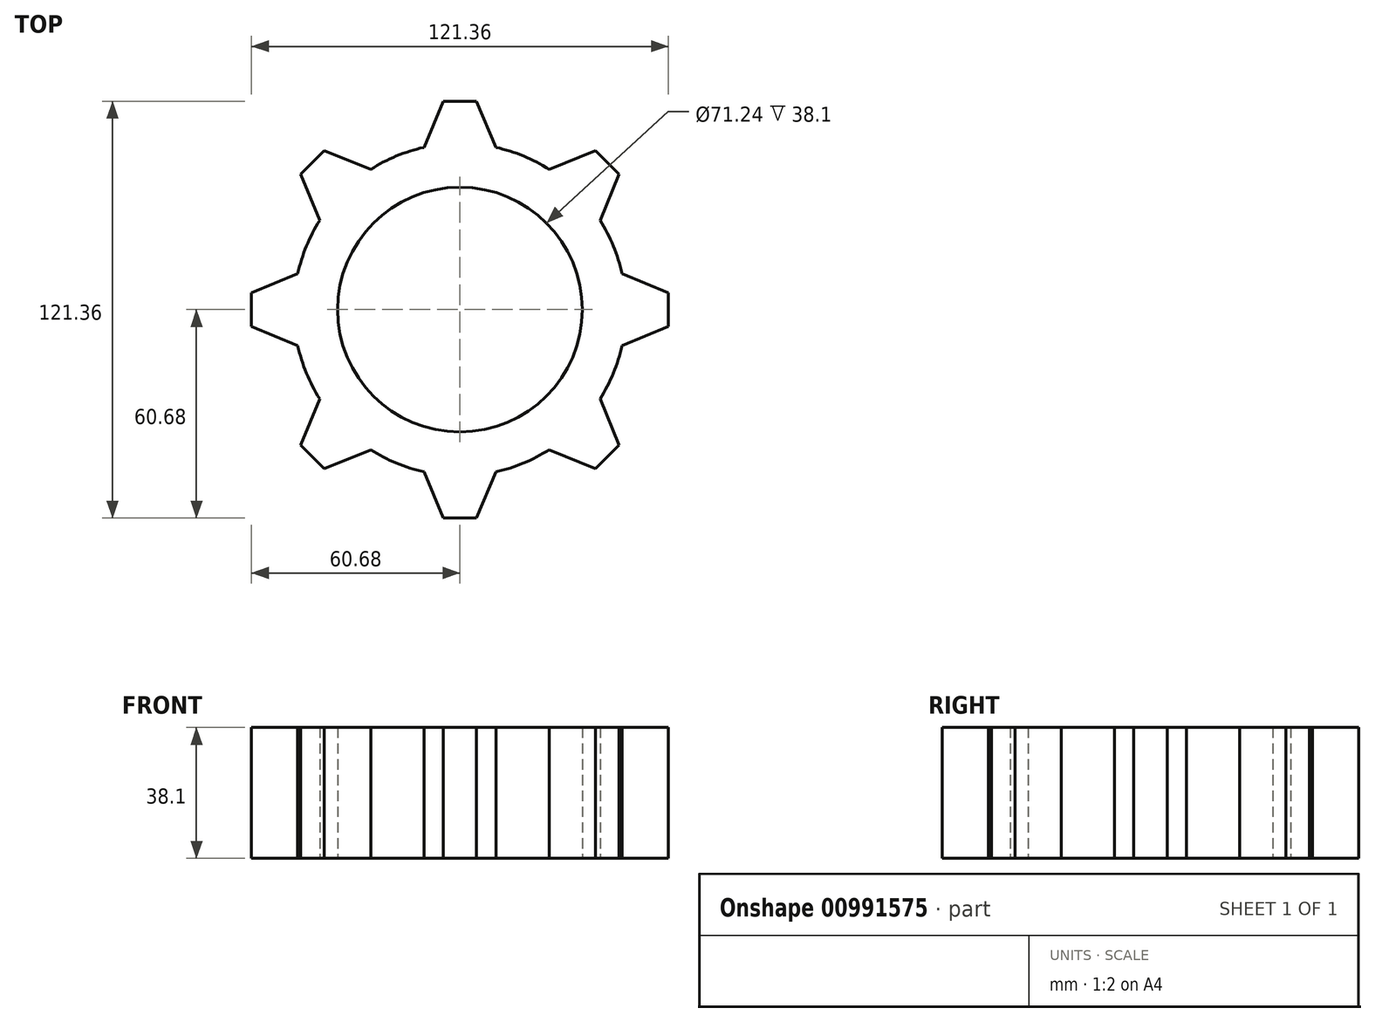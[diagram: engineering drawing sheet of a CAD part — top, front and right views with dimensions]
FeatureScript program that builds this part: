
annotation { "Feature Type Name" : "Feature", "Feature Type Description" : "" }
export const myFeature = defineFeature(function(context is Context, id is Id, definition is map)
    precondition{}
    {
        {
            var Q0;
            Q0=qCreatedBy(makeId("Top.planeOp"),FACE);
            var sketch = newSketch(context, id + "F0", { "sketchPlane" : qUnion([Q0])});
            skCircle(sketch, "E0", {"center": v(0, 0) * mm, "radius": 48.37 * mm});
            skSolve(sketch);
        }
        {
            var Q0;
            Q0=makeQuery(id+"F0.imprint","IMPRINT",FACE,{"disambiguationData":[TD([[makeQuery(id+"F0.imprint","IMPRINT",EDGE,{"derivedFrom":sQuery(id+"F0.wireOp",EDGE,"E0")}),1.0]])]});
            extrude(context, id + "F1", {"entities" : qUnion([Q0]), "depth" : 38.1 * mm, "offsetDistance" : 25.4 * mm});
        }
        {
            var Q0;
            Q0=qCreatedBy(makeId("Top.planeOp"),FACE);
            var sketch = newSketch(context, id + "F2", { "sketchPlane" : qUnion([Q0])});
            skLineSegment(sketch, "E1", {"start": v(42.15, 12.62) * mm, "end": v(60.68, 4.85) * mm});
            skLineSegment(sketch, "E2", {"start": v(60.68, 4.85) * mm, "end": v(60.68, -4.85) * mm});
            skLineSegment(sketch, "E3", {"start": v(60.68, -4.85) * mm, "end": v(42.15, -12.62) * mm});
            skLineSegment(sketch, "E4", {"start": v(42.15, -12.62) * mm, "end": v(42.15, 12.62) * mm});
            skPoint(sketch, "E5.endSnap0", {"position": v(42.15, 0) * mm});
            skLineSegment(sketch, "E6.1.0", {"start": v(39.48, 46.34) * mm, "end": v(46.34, 39.48) * mm});
            skLineSegment(sketch, "E6.1.1", {"start": v(20.88, 38.72) * mm, "end": v(39.48, 46.34) * mm});
            skLineSegment(sketch, "E6.1.2", {"start": v(46.34, 39.48) * mm, "end": v(38.72, 20.88) * mm});
            skLineSegment(sketch, "E6.1.3", {"start": v(38.72, 20.88) * mm, "end": v(20.88, 38.72) * mm});
            skLineSegment(sketch, "E6.2.0", {"start": v(-4.85, 60.68) * mm, "end": v(4.85, 60.68) * mm});
            skLineSegment(sketch, "E6.2.1", {"start": v(-12.62, 42.15) * mm, "end": v(-4.85, 60.68) * mm});
            skLineSegment(sketch, "E6.2.2", {"start": v(4.85, 60.68) * mm, "end": v(12.62, 42.15) * mm});
            skLineSegment(sketch, "E6.2.3", {"start": v(12.62, 42.15) * mm, "end": v(-12.62, 42.15) * mm});
            skLineSegment(sketch, "E6.3.0", {"start": v(-46.34, 39.48) * mm, "end": v(-39.48, 46.34) * mm});
            skLineSegment(sketch, "E6.3.1", {"start": v(-38.72, 20.88) * mm, "end": v(-46.34, 39.48) * mm});
            skLineSegment(sketch, "E6.3.2", {"start": v(-39.48, 46.34) * mm, "end": v(-20.88, 38.72) * mm});
            skLineSegment(sketch, "E6.3.3", {"start": v(-20.88, 38.72) * mm, "end": v(-38.72, 20.88) * mm});
            skLineSegment(sketch, "E6.4.0", {"start": v(-60.68, -4.85) * mm, "end": v(-60.68, 4.85) * mm});
            skLineSegment(sketch, "E6.4.1", {"start": v(-42.15, -12.62) * mm, "end": v(-60.68, -4.85) * mm});
            skLineSegment(sketch, "E6.4.2", {"start": v(-60.68, 4.85) * mm, "end": v(-42.15, 12.62) * mm});
            skLineSegment(sketch, "E6.4.3", {"start": v(-42.15, 12.62) * mm, "end": v(-42.15, -12.62) * mm});
            skLineSegment(sketch, "E6.5.0", {"start": v(-39.48, -46.34) * mm, "end": v(-46.34, -39.48) * mm});
            skLineSegment(sketch, "E6.5.1", {"start": v(-20.88, -38.72) * mm, "end": v(-39.48, -46.34) * mm});
            skLineSegment(sketch, "E6.5.2", {"start": v(-46.34, -39.48) * mm, "end": v(-38.72, -20.88) * mm});
            skLineSegment(sketch, "E6.5.3", {"start": v(-38.72, -20.88) * mm, "end": v(-20.88, -38.72) * mm});
            skLineSegment(sketch, "E6.6.0", {"start": v(4.85, -60.68) * mm, "end": v(-4.85, -60.68) * mm});
            skLineSegment(sketch, "E6.6.1", {"start": v(12.62, -42.15) * mm, "end": v(4.85, -60.68) * mm});
            skLineSegment(sketch, "E6.6.2", {"start": v(-4.85, -60.68) * mm, "end": v(-12.62, -42.15) * mm});
            skLineSegment(sketch, "E6.6.3", {"start": v(-12.62, -42.15) * mm, "end": v(12.62, -42.15) * mm});
            skLineSegment(sketch, "E6.7.0", {"start": v(46.34, -39.48) * mm, "end": v(39.48, -46.34) * mm});
            skLineSegment(sketch, "E6.7.1", {"start": v(38.72, -20.88) * mm, "end": v(46.34, -39.48) * mm});
            skLineSegment(sketch, "E6.7.2", {"start": v(39.48, -46.34) * mm, "end": v(20.88, -38.72) * mm});
            skLineSegment(sketch, "E6.7.3", {"start": v(20.88, -38.72) * mm, "end": v(38.72, -20.88) * mm});
            skPoint(sketch, "E6.center", {"position": v(0, 0) * mm});
            skSolve(sketch);
        }
        {
            var Q0;
            Q0=makeQuery(id+"F2.imprint","IMPRINT",FACE,{"disambiguationData":[TD([[makeQuery(id+"F2.imprint","IMPRINT",EDGE,{"derivedFrom":sQuery(id+"F2.wireOp",EDGE,"E6.2.0")}),-1.0]])]});
            var Q1;
            Q1=makeQuery(id+"F2.imprint","IMPRINT",FACE,{"disambiguationData":[TD([[makeQuery(id+"F2.imprint","IMPRINT",EDGE,{"derivedFrom":sQuery(id+"F2.wireOp",EDGE,"E6.1.0")}),-1.0]])]});
            var Q2;
            Q2=makeQuery(id+"F2.imprint","IMPRINT",FACE,{"disambiguationData":[TD([[makeQuery(id+"F2.imprint","IMPRINT",EDGE,{"derivedFrom":sQuery(id+"F2.wireOp",EDGE,"E1")}),-1.0]])]});
            var Q3;
            Q3=makeQuery(id+"F2.imprint","IMPRINT",FACE,{"disambiguationData":[TD([[makeQuery(id+"F2.imprint","IMPRINT",EDGE,{"derivedFrom":sQuery(id+"F2.wireOp",EDGE,"E6.7.0")}),-1.0]])]});
            var Q4;
            Q4=makeQuery(id+"F2.imprint","IMPRINT",FACE,{"disambiguationData":[TD([[makeQuery(id+"F2.imprint","IMPRINT",EDGE,{"derivedFrom":sQuery(id+"F2.wireOp",EDGE,"E6.6.0")}),-1.0]])]});
            var Q5;
            Q5=makeQuery(id+"F2.imprint","IMPRINT",FACE,{"disambiguationData":[TD([[makeQuery(id+"F2.imprint","IMPRINT",EDGE,{"derivedFrom":sQuery(id+"F2.wireOp",EDGE,"E6.5.0")}),-1.0]])]});
            var Q6;
            Q6=makeQuery(id+"F2.imprint","IMPRINT",FACE,{"disambiguationData":[TD([[makeQuery(id+"F2.imprint","IMPRINT",EDGE,{"derivedFrom":sQuery(id+"F2.wireOp",EDGE,"E6.4.0")}),-1.0]])]});
            var Q7;
            Q7=makeQuery(id+"F2.imprint","IMPRINT",FACE,{"disambiguationData":[TD([[makeQuery(id+"F2.imprint","IMPRINT",EDGE,{"derivedFrom":sQuery(id+"F2.wireOp",EDGE,"E6.3.0")}),-1.0]])]});
            extrude(context, id + "F3", {"entities" : qUnion([Q0, Q1, Q2, Q3, Q4, Q5, Q6, Q7]), "operationType" : NewBodyOperationType.ADD, "depth" : 38.1 * mm, "offsetDistance" : 25.4 * mm});
        }
        {
            var Q0;
            Q0=makeQuery(id+"F3.boolean.opBoolean","MERGE",FACE,{"derivedFrom":[makeQuery(id+"F1.opExtrude","CAP_FACE",FACE,{"disambiguationData":[OSD([sQuery(id+"F0.wireOp",EDGE,"E0")])],"isStart":true}),makeQuery(id+"F3.opExtrude","CAP_FACE",FACE,{"disambiguationData":[OSD([sQuery(id+"F2.wireOp",EDGE,"E1"),sQuery(id+"F2.wireOp",EDGE,"E2"),sQuery(id+"F2.wireOp",EDGE,"E3"),sQuery(id+"F2.wireOp",EDGE,"E4")])],"isStart":true}),makeQuery(id+"F3.opExtrude","CAP_FACE",FACE,{"disambiguationData":[OSD([sQuery(id+"F2.wireOp",EDGE,"E6.1.0"),sQuery(id+"F2.wireOp",EDGE,"E6.1.1"),sQuery(id+"F2.wireOp",EDGE,"E6.1.2"),sQuery(id+"F2.wireOp",EDGE,"E6.1.3")])],"isStart":true}),makeQuery(id+"F3.opExtrude","CAP_FACE",FACE,{"disambiguationData":[OSD([sQuery(id+"F2.wireOp",EDGE,"E6.2.0"),sQuery(id+"F2.wireOp",EDGE,"E6.2.1"),sQuery(id+"F2.wireOp",EDGE,"E6.2.2"),sQuery(id+"F2.wireOp",EDGE,"E6.2.3")])],"isStart":true}),makeQuery(id+"F3.opExtrude","CAP_FACE",FACE,{"disambiguationData":[OSD([sQuery(id+"F2.wireOp",EDGE,"E6.3.0"),sQuery(id+"F2.wireOp",EDGE,"E6.3.1"),sQuery(id+"F2.wireOp",EDGE,"E6.3.2"),sQuery(id+"F2.wireOp",EDGE,"E6.3.3")])],"isStart":true}),makeQuery(id+"F3.opExtrude","CAP_FACE",FACE,{"disambiguationData":[OSD([sQuery(id+"F2.wireOp",EDGE,"E6.4.0"),sQuery(id+"F2.wireOp",EDGE,"E6.4.1"),sQuery(id+"F2.wireOp",EDGE,"E6.4.2"),sQuery(id+"F2.wireOp",EDGE,"E6.4.3")])],"isStart":true}),makeQuery(id+"F3.opExtrude","CAP_FACE",FACE,{"disambiguationData":[OSD([sQuery(id+"F2.wireOp",EDGE,"E6.5.0"),sQuery(id+"F2.wireOp",EDGE,"E6.5.1"),sQuery(id+"F2.wireOp",EDGE,"E6.5.2"),sQuery(id+"F2.wireOp",EDGE,"E6.5.3")])],"isStart":true}),makeQuery(id+"F3.opExtrude","CAP_FACE",FACE,{"disambiguationData":[OSD([sQuery(id+"F2.wireOp",EDGE,"E6.6.0"),sQuery(id+"F2.wireOp",EDGE,"E6.6.1"),sQuery(id+"F2.wireOp",EDGE,"E6.6.2"),sQuery(id+"F2.wireOp",EDGE,"E6.6.3")])],"isStart":true}),makeQuery(id+"F3.opExtrude","CAP_FACE",FACE,{"disambiguationData":[OSD([sQuery(id+"F2.wireOp",EDGE,"E6.7.0"),sQuery(id+"F2.wireOp",EDGE,"E6.7.1"),sQuery(id+"F2.wireOp",EDGE,"E6.7.2"),sQuery(id+"F2.wireOp",EDGE,"E6.7.3")])],"isStart":true})]});
            var sketch = newSketch(context, id + "F4", { "sketchPlane" : qUnion([Q0])});
            skCircle(sketch, "E7", {"center": v(0, 0) * mm, "radius": 35.62 * mm});
            skSolve(sketch);
        }
        {
            var Q0;
            Q0=makeQuery(id+"F4.imprint","IMPRINT",FACE,{"disambiguationData":[TD([[makeQuery(id+"F4.imprint","IMPRINT",EDGE,{"derivedFrom":sQuery(id+"F4.wireOp",EDGE,"E7")}),1.0]])]});
            extrude(context, id + "F5", {"entities" : qUnion([Q0]), "operationType" : NewBodyOperationType.REMOVE, "oppositeDirection" : true, "depth" : 66.3 * mm, "offsetDistance" : 25.4 * mm});
        }
    });
